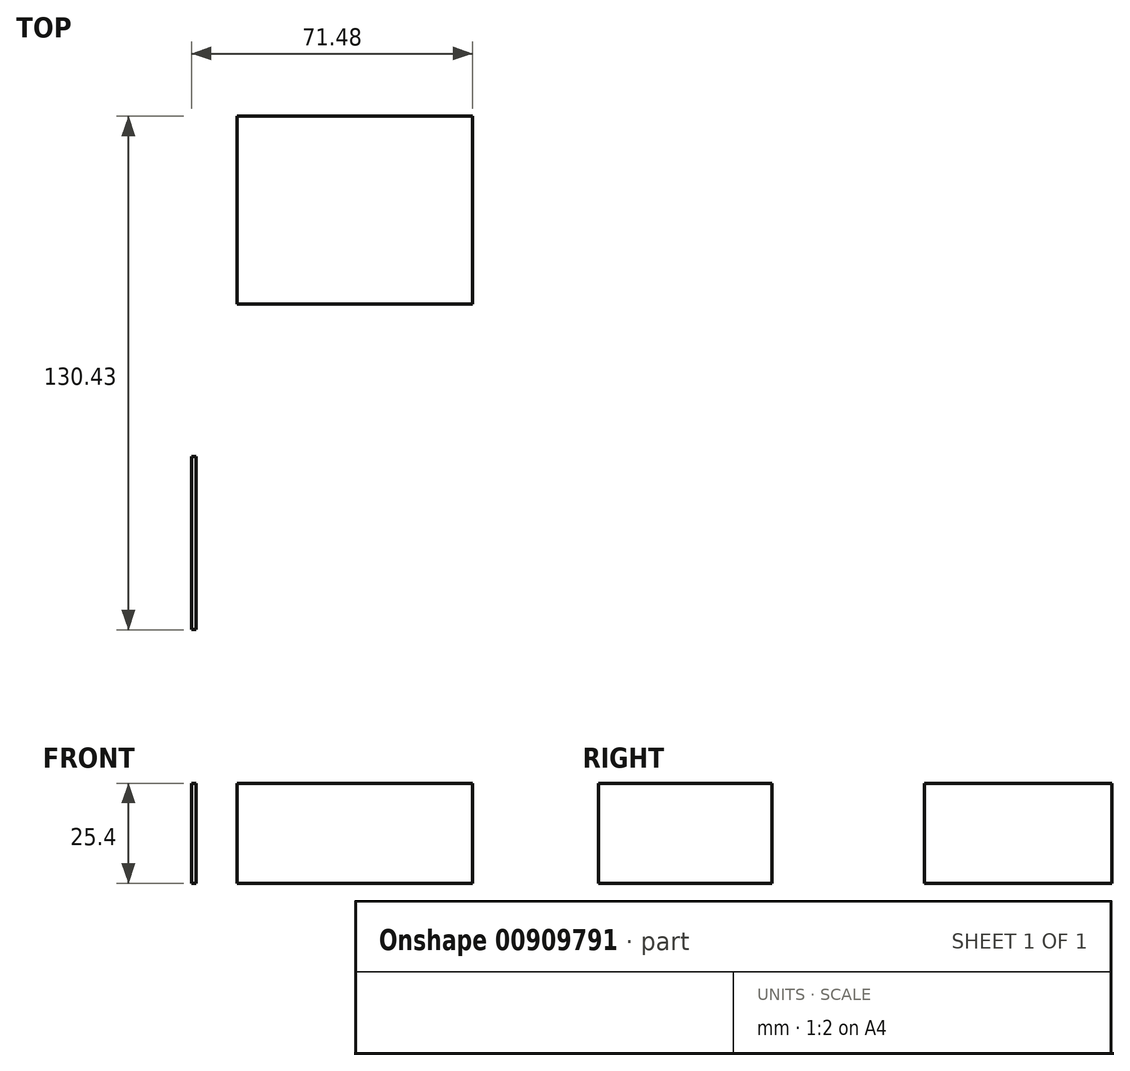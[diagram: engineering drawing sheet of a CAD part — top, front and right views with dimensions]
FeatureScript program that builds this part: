
annotation { "Feature Type Name" : "Feature", "Feature Type Description" : "" }
export const myFeature = defineFeature(function(context is Context, id is Id, definition is map)
    precondition{}
    {
        {
            var Q0;
            Q0=qCreatedBy(makeId("Top.planeOp"),FACE);
            var sketch = newSketch(context, id + "F0", { "sketchPlane" : qUnion([Q0])});
            skLineSegment(sketch, "E0.bottom", {"start": v(-70.3, -82.77) * mm, "end": v(-71.48, -82.77) * mm});
            skLineSegment(sketch, "E0.top", {"start": v(-70.3, -38.73) * mm, "end": v(-71.48, -38.73) * mm});
            skLineSegment(sketch, "E0.left", {"start": v(-70.3, -82.77) * mm, "end": v(-70.3, -38.73) * mm});
            skLineSegment(sketch, "E0.right", {"start": v(-71.48, -82.77) * mm, "end": v(-71.48, -38.73) * mm});
            skLineSegment(sketch, "E1.bottom", {"start": v(-59.92, 0) * mm, "end": v(0, 0) * mm});
            skLineSegment(sketch, "E1.top", {"start": v(-59.92, 47.66) * mm, "end": v(0, 47.66) * mm});
            skLineSegment(sketch, "E1.left", {"start": v(-59.92, 0) * mm, "end": v(-59.92, 47.66) * mm});
            skLineSegment(sketch, "E1.right", {"start": v(0, 0) * mm, "end": v(0, 47.66) * mm});
            skSolve(sketch);
        }
        {
            var Q0;
            Q0 = qSketchRegion(id + "F0", true);
            extrude(context, id + "F1", {"entities" : qUnion([Q0]), "depth" : 25.4 * mm, "offsetDistance" : 25.4 * mm});
        }
    });
